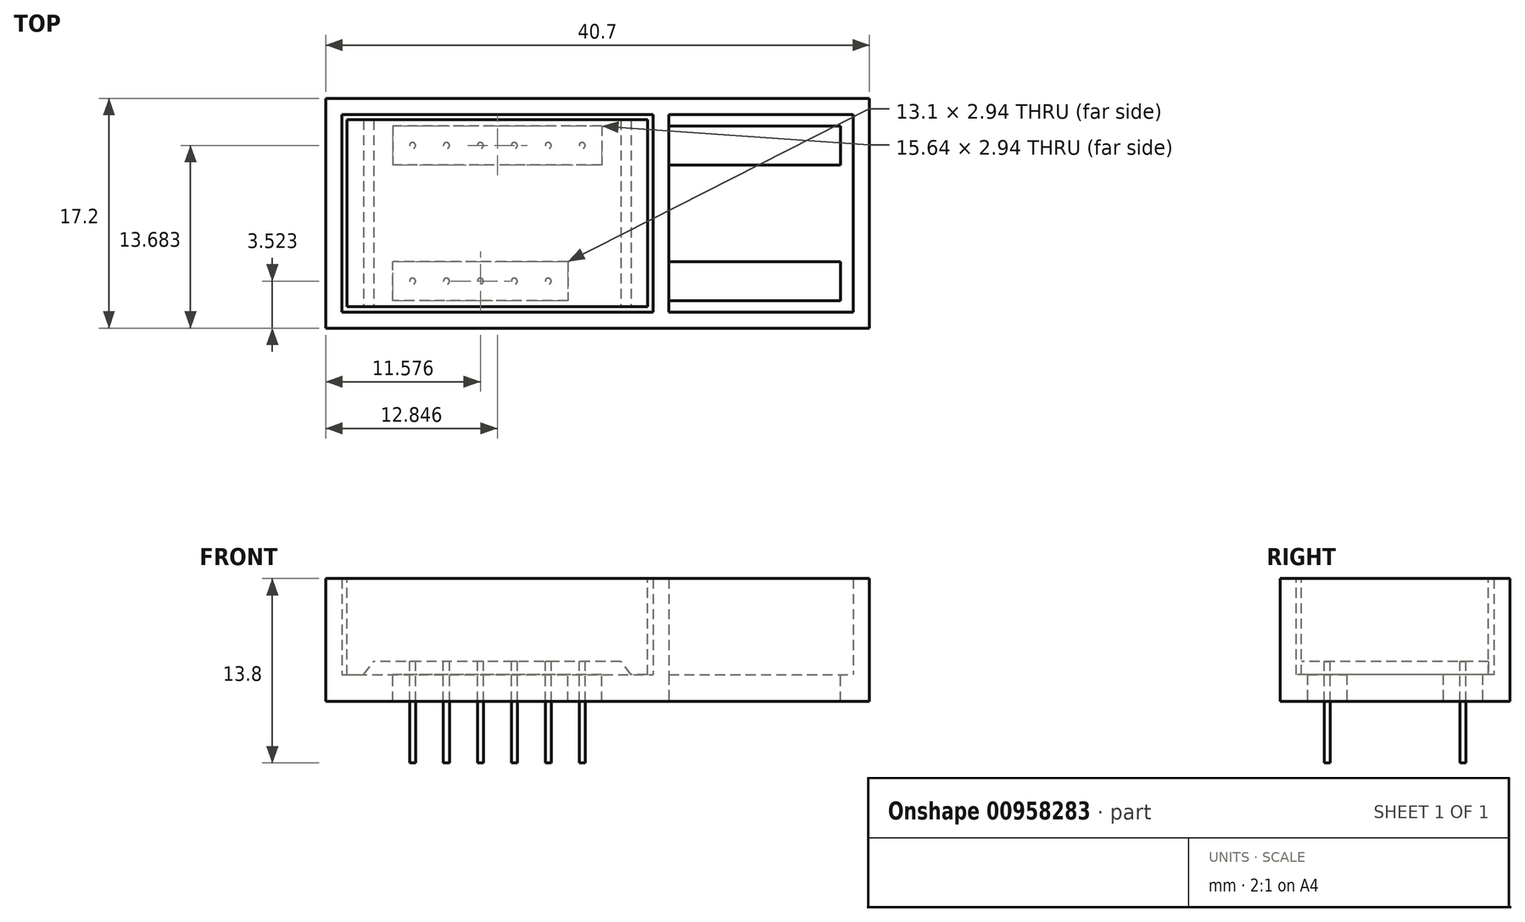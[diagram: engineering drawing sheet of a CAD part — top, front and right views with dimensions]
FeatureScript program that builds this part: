
annotation { "Feature Type Name" : "Feature", "Feature Type Description" : "" }
export const myFeature = defineFeature(function(context is Context, id is Id, definition is map)
    precondition{}
    {
        {
            var Q0;
            Q0=qCreatedBy(makeId("Top.planeOp"),FACE);
            cPlane(context, id + "F0", {"entities" : qUnion([Q0]), "cplaneType" : CPlaneType.OFFSET, "offset" : 0 * mm, "oppositeDirection" : true, "width" : 150 * mm, "height" : 150 * mm});
        }
        {
            var Q0;
            Q0=qCreatedBy(id+"F0.planeOp",FACE);
            cPlane(context, id + "F1", {"entities" : qUnion([Q0]), "cplaneType" : CPlaneType.OFFSET, "offset" : 1 * mm, "width" : 150 * mm, "height" : 150 * mm});
        }
        {
            var Q0;
            Q0=qCreatedBy(id+"F0.planeOp",FACE);
            cPlane(context, id + "F2", {"entities" : qUnion([Q0]), "cplaneType" : CPlaneType.OFFSET, "offset" : 7.2 * mm, "width" : 150 * mm, "height" : 150 * mm});
        }
        {
            var Q0;
            Q0=qCreatedBy(id+"F0.planeOp",FACE);
            cPlane(context, id + "F3", {"entities" : qUnion([Q0]), "cplaneType" : CPlaneType.OFFSET, "offset" : 6.6 * mm, "oppositeDirection" : true, "width" : 150 * mm, "height" : 150 * mm});
        }
        {
            var Q0;
            Q0=qCreatedBy(id+"F2.planeOp",FACE);
            var sketch = newSketch(context, id + "F4", { "sketchPlane" : qUnion([Q0])});
            skLineSegment(sketch, "E0.bottom", {"start": v(-106.65, 26.58) * mm, "end": v(-84.15, 26.58) * mm});
            skLineSegment(sketch, "E0.top", {"start": v(-106.65, 12.58) * mm, "end": v(-84.15, 12.58) * mm});
            skLineSegment(sketch, "E0.left", {"start": v(-106.65, 26.58) * mm, "end": v(-106.65, 12.58) * mm});
            skLineSegment(sketch, "E0.right", {"start": v(-84.15, 26.58) * mm, "end": v(-84.15, 12.58) * mm});
            skLineSegment(sketch, "E1", {"start": v(-95.4, 28.14) * mm, "end": v(-95.4, 9.66) * mm, "construction": true});
            skSolve(sketch);
        }
        {
            var Q0;
            Q0=qCreatedBy(id+"F1.planeOp",FACE);
            var sketch = newSketch(context, id + "F5", { "sketchPlane" : qUnion([Q0])});
            skLineSegment(sketch, "E2", {"start": v(-135.23, 24.66) * mm, "end": v(-81.77, 24.66) * mm, "construction": true});
            skCircle(sketch, "E3", {"center": v(-101.75, 24.66) * mm, "radius": 0.23 * mm});
            skLineSegment(sketch, "E4", {"start": v(-135.23, 14.5) * mm, "end": v(-81.77, 14.5) * mm, "construction": true});
            skLineSegment(sketch, "E5", {"start": v(-89.05, 29.01) * mm, "end": v(-89.05, 8.16) * mm, "construction": true});
            skLineSegment(sketch, "E6", {"start": v(-96.67, 29.01) * mm, "end": v(-96.67, 8.16) * mm, "construction": true});
            skLineSegment(sketch, "E7", {"start": v(-101.75, 29.01) * mm, "end": v(-101.75, 8.16) * mm, "construction": true});
            skLineSegment(sketch, "E8", {"start": v(-99.21, 29.01) * mm, "end": v(-99.21, 8.16) * mm, "construction": true});
            skLineSegment(sketch, "E9", {"start": v(-94.13, 29.01) * mm, "end": v(-94.13, 8.16) * mm, "construction": true});
            skLineSegment(sketch, "E10", {"start": v(-91.6, 29.01) * mm, "end": v(-91.6, 8.16) * mm, "construction": true});
            skCircle(sketch, "E11", {"center": v(-99.21, 24.66) * mm, "radius": 0.23 * mm});
            skCircle(sketch, "E12", {"center": v(-96.67, 24.66) * mm, "radius": 0.23 * mm});
            skCircle(sketch, "E13", {"center": v(-101.75, 14.5) * mm, "radius": 0.23 * mm});
            skCircle(sketch, "E14", {"center": v(-99.21, 14.5) * mm, "radius": 0.23 * mm});
            skCircle(sketch, "E15", {"center": v(-96.67, 14.5) * mm, "radius": 0.23 * mm});
            skCircle(sketch, "E16", {"center": v(-94.13, 24.66) * mm, "radius": 0.23 * mm});
            skCircle(sketch, "E17", {"center": v(-91.6, 24.66) * mm, "radius": 0.23 * mm});
            skCircle(sketch, "E18", {"center": v(-94.13, 14.5) * mm, "radius": 0.23 * mm});
            skCircle(sketch, "E19", {"center": v(-91.6, 14.5) * mm, "radius": 0.23 * mm});
            skCircle(sketch, "E20", {"center": v(-89.05, 24.66) * mm, "radius": 0.23 * mm});
            skLineSegment(sketch, "E21", {"start": v(-109.1, 19.58) * mm, "end": v(-80.5, 19.58) * mm, "construction": true});
            skSolve(sketch);
        }
        {
            var Q0;
            Q0=makeQuery(id+"F4.imprint","IMPRINT",FACE,{"disambiguationData":[TD([[makeQuery(id+"F4.imprint","IMPRINT",EDGE,{"derivedFrom":sQuery(id+"F4.wireOp",EDGE,"E0.bottom")}),-1.0]])]});
            var Q1;
            Q1=qCreatedBy(id+"F1.planeOp",FACE);
            extrude(context, id + "F6", {"entities" : qUnion([Q0]), "endBound" : BoundingType.UP_TO_SURFACE, "oppositeDirection" : true, "depth" : 25 * mm, "endBoundEntityFace" : qUnion([Q1]), "offsetDistance" : 25 * mm});
        }
        {
            var Q0;
            Q0=makeQuery(id+"F5.imprint","IMPRINT",FACE,{"disambiguationData":[TD([[makeQuery(id+"F5.imprint","IMPRINT",EDGE,{"derivedFrom":sQuery(id+"F5.wireOp",EDGE,"f23e19de-ad88-4ec4-ac5d-b15bf174d9e4")}),1.0]])]});
            var Q1;
            Q1=makeQuery(id+"F5.imprint","IMPRINT",FACE,{"disambiguationData":[TD([[makeQuery(id+"F5.imprint","IMPRINT",EDGE,{"derivedFrom":sQuery(id+"F5.wireOp",EDGE,"E17")}),1.0]])]});
            var Q2;
            Q2=makeQuery(id+"F5.imprint","IMPRINT",FACE,{"disambiguationData":[TD([[makeQuery(id+"F5.imprint","IMPRINT",EDGE,{"derivedFrom":sQuery(id+"F5.wireOp",EDGE,"E16")}),1.0]])]});
            var Q3;
            Q3=makeQuery(id+"F5.imprint","IMPRINT",FACE,{"disambiguationData":[TD([[makeQuery(id+"F5.imprint","IMPRINT",EDGE,{"derivedFrom":sQuery(id+"F5.wireOp",EDGE,"E12")}),1.0]])]});
            var Q4;
            Q4=makeQuery(id+"F5.imprint","IMPRINT",FACE,{"disambiguationData":[TD([[makeQuery(id+"F5.imprint","IMPRINT",EDGE,{"derivedFrom":sQuery(id+"F5.wireOp",EDGE,"E11")}),1.0]])]});
            var Q5;
            Q5=makeQuery(id+"F5.imprint","IMPRINT",FACE,{"disambiguationData":[TD([[makeQuery(id+"F5.imprint","IMPRINT",EDGE,{"derivedFrom":sQuery(id+"F5.wireOp",EDGE,"E3")}),1.0]])]});
            var Q6;
            Q6=makeQuery(id+"F5.imprint","IMPRINT",FACE,{"disambiguationData":[TD([[makeQuery(id+"F5.imprint","IMPRINT",EDGE,{"derivedFrom":sQuery(id+"F5.wireOp",EDGE,"E13")}),1.0]])]});
            var Q7;
            Q7=makeQuery(id+"F5.imprint","IMPRINT",FACE,{"disambiguationData":[TD([[makeQuery(id+"F5.imprint","IMPRINT",EDGE,{"derivedFrom":sQuery(id+"F5.wireOp",EDGE,"E14")}),1.0]])]});
            var Q8;
            Q8=makeQuery(id+"F5.imprint","IMPRINT",FACE,{"disambiguationData":[TD([[makeQuery(id+"F5.imprint","IMPRINT",EDGE,{"derivedFrom":sQuery(id+"F5.wireOp",EDGE,"E15")}),1.0]])]});
            var Q9;
            Q9=makeQuery(id+"F5.imprint","IMPRINT",FACE,{"disambiguationData":[TD([[makeQuery(id+"F5.imprint","IMPRINT",EDGE,{"derivedFrom":sQuery(id+"F5.wireOp",EDGE,"E18")}),1.0]])]});
            var Q10;
            Q10=makeQuery(id+"F5.imprint","IMPRINT",FACE,{"disambiguationData":[TD([[makeQuery(id+"F5.imprint","IMPRINT",EDGE,{"derivedFrom":sQuery(id+"F5.wireOp",EDGE,"E19")}),1.0]])]});
            var Q11;
            Q11=makeQuery(id+"F5.imprint","IMPRINT",FACE,{"disambiguationData":[TD([[makeQuery(id+"F5.imprint","IMPRINT",EDGE,{"derivedFrom":sQuery(id+"F5.wireOp",EDGE,"E20")}),1.0]])]});
            var Q12;
            Q12=qCreatedBy(id+"F3.planeOp",FACE);
            extrude(context, id + "F7", {"entities" : qUnion([Q0, Q1, Q2, Q3, Q4, Q5, Q6, Q7, Q8, Q9, Q10, Q11]), "operationType" : NewBodyOperationType.ADD, "endBound" : BoundingType.UP_TO_SURFACE, "oppositeDirection" : true, "depth" : 25 * mm, "endBoundEntityFace" : qUnion([Q12]), "offsetDistance" : 25 * mm});
        }
        {
            var Q0;
            Q0=makeQuery(id+"F6.opExtrude","SWEPT_FACE",FACE,{"disambiguationData":[OSD([sQuery(id+"F4.wireOp",EDGE,"E0.top")])]});
            cPlane(context, id + "F8", {"entities" : qUnion([Q0]), "cplaneType" : CPlaneType.OFFSET, "offset" : 0 * mm, "width" : 150 * mm, "height" : 150 * mm});
        }
        {
            var Q0;
            Q0=qCreatedBy(id+"F8.planeOp",FACE);
            var sketch = newSketch(context, id + "F9", { "sketchPlane" : qUnion([Q0])});
            skLineSegment(sketch, "E22", {"start": v(-106.65, 1) * mm, "end": v(-106.65, 0) * mm});
            skLineSegment(sketch, "E23", {"start": v(-106.65, 0) * mm, "end": v(-105.42, 0) * mm});
            skLineSegment(sketch, "E24", {"start": v(-105.42, 0) * mm, "end": v(-104.65, 1) * mm});
            skLineSegment(sketch, "E25", {"start": v(-104.65, 1) * mm, "end": v(-106.65, 1) * mm});
            skLineSegment(sketch, "E26", {"start": v(-95.4, 13.32) * mm, "end": v(-95.4, -3.51) * mm, "construction": true});
            skLineSegment(sketch, "E27.MirrorCS", {"start": v(-85.39, 0) * mm, "end": v(-86.16, 1) * mm});
            skLineSegment(sketch, "E28.MirrorCS", {"start": v(-86.16, 1) * mm, "end": v(-84.15, 1) * mm});
            skLineSegment(sketch, "E29.MirrorCS", {"start": v(-84.15, 1) * mm, "end": v(-84.15, 0) * mm});
            skLineSegment(sketch, "E30.MirrorCS", {"start": v(-84.15, 0) * mm, "end": v(-85.39, 0) * mm});
            skSolve(sketch);
        }
        {
            var Q0;
            Q0=makeQuery(id+"F9.imprint","IMPRINT",FACE,{"disambiguationData":[TD([[makeQuery(id+"F9.imprint","IMPRINT",EDGE,{"derivedFrom":sQuery(id+"F9.wireOp",EDGE,"E22")}),1.0]])]});
            var Q1;
            Q1=makeQuery(id+"F9.imprint","IMPRINT",FACE,{"disambiguationData":[TD([[makeQuery(id+"F9.imprint","IMPRINT",EDGE,{"derivedFrom":sQuery(id+"F9.wireOp",EDGE,"E27.MirrorCS")}),-1.0]])]});
            var Q2;
            Q2=makeQuery(id+"F6.opExtrude","SWEPT_FACE",FACE,{"disambiguationData":[OSD([sQuery(id+"F4.wireOp",EDGE,"E0.bottom")])]});
            extrude(context, id + "F10", {"entities" : qUnion([Q0, Q1]), "operationType" : NewBodyOperationType.ADD, "endBound" : BoundingType.UP_TO_SURFACE, "oppositeDirection" : true, "depth" : 25 * mm, "endBoundEntityFace" : qUnion([Q2]), "offsetDistance" : 25 * mm});
        }
        {
            var Q0;
            Q0=qCreatedBy(id+"F0.planeOp",FACE);
            var sketch = newSketch(context, id + "F11", { "sketchPlane" : qUnion([Q0])});
            skLineSegment(sketch, "E31.bottom", {"start": v(-107.05, 26.98) * mm, "end": v(-83.75, 26.98) * mm});
            skLineSegment(sketch, "E31.top", {"start": v(-107.05, 12.18) * mm, "end": v(-83.75, 12.18) * mm});
            skLineSegment(sketch, "E31.left", {"start": v(-107.05, 26.98) * mm, "end": v(-107.05, 12.18) * mm});
            skLineSegment(sketch, "E31.right", {"start": v(-83.75, 26.98) * mm, "end": v(-83.75, 12.18) * mm});
            skLineSegment(sketch, "E32.bottom", {"start": v(-108.25, 28.18) * mm, "end": v(-82.55, 28.18) * mm});
            skLineSegment(sketch, "E32.top", {"start": v(-108.25, 10.98) * mm, "end": v(-82.55, 10.98) * mm});
            skLineSegment(sketch, "E32.left", {"start": v(-108.25, 28.18) * mm, "end": v(-108.25, 10.98) * mm});
            skLineSegment(sketch, "E32.right", {"start": v(-82.55, 28.18) * mm, "end": v(-82.55, 10.98) * mm});
            skLineSegment(sketch, "E33", {"start": v(-95.4, 22.12) * mm, "end": v(-95.4, 16.67) * mm, "construction": true});
            skLineSegment(sketch, "E34", {"start": v(-92.27, 19.58) * mm, "end": v(-97.7, 19.58) * mm, "construction": true});
            skLineSegment(sketch, "E35.bottom", {"start": v(-87.58, 26.13) * mm, "end": v(-103.22, 26.13) * mm});
            skLineSegment(sketch, "E35.top", {"start": v(-87.58, 23.2) * mm, "end": v(-103.22, 23.2) * mm});
            skLineSegment(sketch, "E35.left", {"start": v(-87.58, 26.13) * mm, "end": v(-87.58, 23.2) * mm});
            skLineSegment(sketch, "E35.right", {"start": v(-103.22, 26.13) * mm, "end": v(-103.22, 23.2) * mm});
            skLineSegment(sketch, "E36", {"start": v(-95.4, 27.27) * mm, "end": v(-95.4, 22.72) * mm, "construction": true});
            skLineSegment(sketch, "E37.bottom", {"start": v(-100.48, 23.4) * mm, "end": v(-103.02, 23.4) * mm, "construction": true});
            skLineSegment(sketch, "E37.top", {"start": v(-100.48, 25.93) * mm, "end": v(-103.02, 25.93) * mm, "construction": true});
            skLineSegment(sketch, "E37.left", {"start": v(-103.02, 23.4) * mm, "end": v(-103.02, 25.93) * mm, "construction": true});
            skLineSegment(sketch, "E37.right", {"start": v(-100.48, 23.4) * mm, "end": v(-100.48, 25.93) * mm, "construction": true});
            skLineSegment(sketch, "E38.MirrorCS", {"start": v(-90.12, 15.97) * mm, "end": v(-103.22, 15.97) * mm});
            skLineSegment(sketch, "E39.MirrorCS", {"start": v(-90.12, 13.03) * mm, "end": v(-103.22, 13.03) * mm});
            skLineSegment(sketch, "E40.MirrorCS", {"start": v(-103.22, 13.03) * mm, "end": v(-103.22, 15.97) * mm});
            skLineSegment(sketch, "E41", {"start": v(-90.12, 15.97) * mm, "end": v(-90.12, 13.03) * mm});
            skSolve(sketch);
        }
        {
            var Q0;
            Q0=makeQuery(id+"F11.imprint","IMPRINT",FACE,{"disambiguationData":[TD([[makeQuery(id+"F11.imprint","IMPRINT",EDGE,{"derivedFrom":sQuery(id+"F11.wireOp",EDGE,"E31.bottom")}),1.0]])]});
            var Q1;
            Q1=qCreatedBy(id+"F2.planeOp",FACE);
            extrude(context, id + "F12", {"entities" : qUnion([Q0]), "endBound" : BoundingType.UP_TO_SURFACE, "depth" : 25 * mm, "endBoundEntityFace" : qUnion([Q1]), "offsetDistance" : 25 * mm});
        }
        {
            var Q0;
            Q0=makeQuery(id+"F11.imprint","IMPRINT",FACE,{"disambiguationData":[TD([[makeQuery(id+"F11.imprint","IMPRINT",EDGE,{"derivedFrom":sQuery(id+"F11.wireOp",EDGE,"E31.bottom")}),-1.0]])]});
            var Q1;
            Q1=makeQuery(id+"F11.imprint","IMPRINT",FACE,{"disambiguationData":[TD([[makeQuery(id+"F11.imprint","IMPRINT",EDGE,{"derivedFrom":sQuery(id+"F11.wireOp",EDGE,"E31.bottom")}),1.0]])]});
            extrude(context, id + "F13", {"entities" : qUnion([Q0, Q1]), "operationType" : NewBodyOperationType.ADD, "oppositeDirection" : true, "depth" : 2 * mm, "offsetDistance" : 25 * mm});
        }
        {
            var Q0;
            Q0=qCreatedBy(id+"F0.planeOp",FACE);
            var sketch = newSketch(context, id + "F14", { "sketchPlane" : qUnion([Q0])});
            skLineSegment(sketch, "E42.bottom", {"start": v(-108.25, 28.18) * mm, "end": v(-67.55, 28.18) * mm});
            skLineSegment(sketch, "E42.top", {"start": v(-108.25, 10.98) * mm, "end": v(-67.55, 10.98) * mm});
            skLineSegment(sketch, "E42.right", {"start": v(-67.55, 28.18) * mm, "end": v(-67.55, 10.98) * mm});
            skLineSegment(sketch, "E43.bottom", {"start": v(-82.8, 15.97) * mm, "end": v(-69.7, 15.97) * mm});
            skLineSegment(sketch, "E43.top", {"start": v(-82.8, 13.03) * mm, "end": v(-69.7, 13.03) * mm});
            skLineSegment(sketch, "E43.left", {"start": v(-82.8, 15.97) * mm, "end": v(-82.8, 13.03) * mm});
            skLineSegment(sketch, "E43.right", {"start": v(-69.7, 15.97) * mm, "end": v(-69.7, 13.03) * mm});
            skLineSegment(sketch, "E44", {"start": v(-108.25, 28.18) * mm, "end": v(-108.25, 10.98) * mm});
            skLineSegment(sketch, "E45", {"start": v(-68.75, 26.98) * mm, "end": v(-107.05, 26.98) * mm});
            skLineSegment(sketch, "E46", {"start": v(-107.05, 26.98) * mm, "end": v(-107.05, 12.18) * mm});
            skLineSegment(sketch, "E47", {"start": v(-107.05, 12.18) * mm, "end": v(-68.75, 12.18) * mm});
            skLineSegment(sketch, "E48", {"start": v(-68.75, 26.98) * mm, "end": v(-68.75, 12.18) * mm});
            skLineSegment(sketch, "E49", {"start": v(-76.25, 22.15) * mm, "end": v(-76.25, 16.97) * mm, "construction": true});
            skLineSegment(sketch, "E50", {"start": v(-74.25, 19.58) * mm, "end": v(-80.64, 19.58) * mm, "construction": true});
            skLineSegment(sketch, "E51.MirrorCS", {"start": v(-82.8, 23.2) * mm, "end": v(-69.7, 23.2) * mm});
            skLineSegment(sketch, "E52.MirrorCS", {"start": v(-82.8, 23.2) * mm, "end": v(-82.8, 26.13) * mm});
            skLineSegment(sketch, "E53.MirrorCS", {"start": v(-82.8, 26.13) * mm, "end": v(-69.7, 26.13) * mm});
            skLineSegment(sketch, "E54.MirrorCS", {"start": v(-69.7, 23.2) * mm, "end": v(-69.7, 26.13) * mm});
            skLineSegment(sketch, "E55.bottom", {"start": v(-103.22, 26.13) * mm, "end": v(-87.58, 26.13) * mm});
            skLineSegment(sketch, "E55.top", {"start": v(-103.22, 23.2) * mm, "end": v(-87.58, 23.2) * mm});
            skLineSegment(sketch, "E55.left", {"start": v(-103.22, 26.13) * mm, "end": v(-103.22, 23.2) * mm});
            skLineSegment(sketch, "E55.right", {"start": v(-87.58, 26.13) * mm, "end": v(-87.58, 23.2) * mm});
            skLineSegment(sketch, "E56.bottom", {"start": v(-103.22, 15.97) * mm, "end": v(-90.12, 15.97) * mm});
            skLineSegment(sketch, "E56.top", {"start": v(-103.22, 13.03) * mm, "end": v(-90.12, 13.03) * mm});
            skLineSegment(sketch, "E56.left", {"start": v(-103.22, 15.97) * mm, "end": v(-103.22, 13.03) * mm});
            skLineSegment(sketch, "E56.right", {"start": v(-90.12, 15.97) * mm, "end": v(-90.12, 13.03) * mm});
            skSolve(sketch);
        }
        {
            var Q0;
            Q0=makeQuery(id+"F14.imprint","IMPRINT",FACE,{"disambiguationData":[TD([[makeQuery(id+"F14.imprint","IMPRINT",EDGE,{"derivedFrom":sQuery(id+"F14.wireOp",EDGE,"E42.bottom")}),-1.0]])]});
            var Q1;
            Q1=qCreatedBy(id+"F2.planeOp",FACE);
            extrude(context, id + "F15", {"entities" : qUnion([Q0]), "endBound" : BoundingType.UP_TO_SURFACE, "depth" : 25 * mm, "endBoundEntityFace" : qUnion([Q1]), "offsetDistance" : 25 * mm});
        }
        {
            var Q0;
            Q0=makeQuery(id+"F14.imprint","IMPRINT",FACE,{"disambiguationData":[TD([[makeQuery(id+"F14.imprint","IMPRINT",EDGE,{"derivedFrom":sQuery(id+"F14.wireOp",EDGE,"E43.bottom")}),1.0]])]});
            var Q1;
            Q1=makeQuery(id+"F14.imprint","IMPRINT",FACE,{"disambiguationData":[TD([[makeQuery(id+"F14.imprint","IMPRINT",EDGE,{"derivedFrom":sQuery(id+"F14.wireOp",EDGE,"E42.bottom")}),-1.0]])]});
            extrude(context, id + "F16", {"entities" : qUnion([Q0, Q1]), "operationType" : NewBodyOperationType.ADD, "oppositeDirection" : true, "depth" : 2 * mm, "offsetDistance" : 25 * mm});
        }
    });
